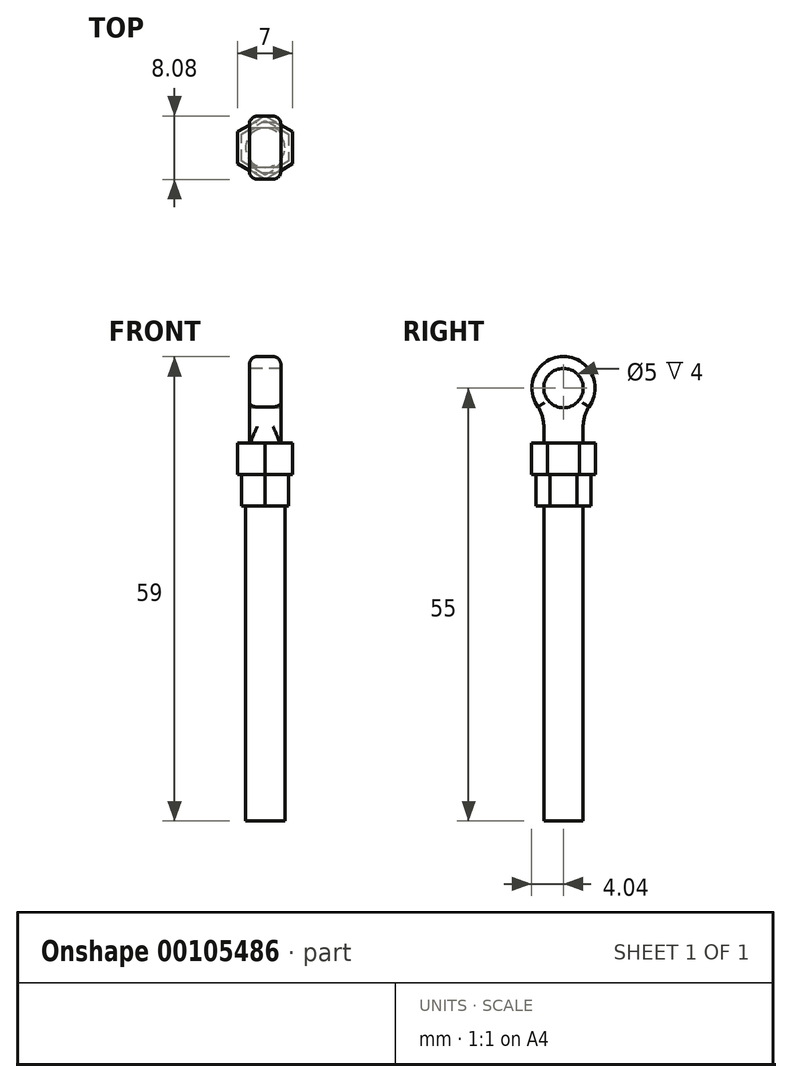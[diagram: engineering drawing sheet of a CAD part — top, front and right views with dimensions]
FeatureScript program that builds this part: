
annotation { "Feature Type Name" : "Feature", "Feature Type Description" : "" }
export const myFeature = defineFeature(function(context is Context, id is Id, definition is map)
    precondition{}
    {
        {
            var Q0;
            Q0=qCreatedBy(makeId("Top.planeOp"),FACE);
            var sketch = newSketch(context, id + "F0", { "sketchPlane" : qUnion([Q0])});
            skCircle(sketch, "E0", {"center": v(0, 0) * mm, "radius": 2.5 * mm});
            skSolve(sketch);
        }
        {
            var Q0;
            Q0=makeQuery(id+"F0.imprint","IMPRINT",FACE,{"disambiguationData":[TD([[makeQuery(id+"F0.imprint","IMPRINT",EDGE,{"derivedFrom":sQuery(id+"F0.wireOp",EDGE,"E0")}),1.0]])]});
            extrude(context, id + "F1", {"entities" : qUnion([Q0]), "depth" : 40 * mm});
        }
        {
            var Q0;
            Q0=makeQuery(id+"F1.opExtrude","CAP_FACE",FACE,{"disambiguationData":[OSD([sQuery(id+"F0.wireOp",EDGE,"E0")])],"isStart":false});
            var sketch = newSketch(context, id + "F2", { "sketchPlane" : qUnion([Q0])});
            skCircle(sketch, "E1.cCircle", {"center": v(0, 0) * mm, "radius": 3 * mm, "construction": true});
            skLineSegment(sketch, "E1.0", {"start": v(3, 1.73) * mm, "end": v(3, -1.73) * mm});
            skLineSegment(sketch, "E1.1", {"start": v(3, -1.73) * mm, "end": v(0, -3.46) * mm});
            skLineSegment(sketch, "E1.2", {"start": v(0, -3.46) * mm, "end": v(-3, -1.73) * mm});
            skLineSegment(sketch, "E1.3", {"start": v(-3, -1.73) * mm, "end": v(-3, 1.73) * mm});
            skLineSegment(sketch, "E1.4", {"start": v(-3, 1.73) * mm, "end": v(0, 3.46) * mm});
            skLineSegment(sketch, "E1.5", {"start": v(0, 3.46) * mm, "end": v(3, 1.73) * mm});
            skPoint(sketch, "E1.0.midPoint", {"position": v(3, 0) * mm});
            skSolve(sketch);
        }
        {
            var Q0;
            Q0=qSketchRegion(id+"F2",true);
            extrude(context, id + "F3", {"entities" : qUnion([Q0]), "operationType" : NewBodyOperationType.ADD, "depth" : 4 * mm});
        }
        {
            var Q0;
            Q0=makeQuery(id+"F3.opExtrude","CAP_FACE",FACE,{"disambiguationData":[OSD([sQuery(id+"F2.wireOp",EDGE,"E1.0"),sQuery(id+"F2.wireOp",EDGE,"E1.1"),sQuery(id+"F2.wireOp",EDGE,"E1.2"),sQuery(id+"F2.wireOp",EDGE,"E1.3"),sQuery(id+"F2.wireOp",EDGE,"E1.4"),sQuery(id+"F2.wireOp",EDGE,"E1.5")])],"isStart":false});
            var sketch = newSketch(context, id + "F4", { "sketchPlane" : qUnion([Q0])});
            skCircle(sketch, "E2.cCircle", {"center": v(0, 0) * mm, "radius": 3.5 * mm, "construction": true});
            skLineSegment(sketch, "E2.0", {"start": v(3.5, 2.02) * mm, "end": v(3.5, -2.02) * mm});
            skLineSegment(sketch, "E2.1", {"start": v(3.5, -2.02) * mm, "end": v(0, -4.04) * mm});
            skLineSegment(sketch, "E2.2", {"start": v(0, -4.04) * mm, "end": v(-3.5, -2.02) * mm});
            skLineSegment(sketch, "E2.3", {"start": v(-3.5, -2.02) * mm, "end": v(-3.5, 2.02) * mm});
            skLineSegment(sketch, "E2.4", {"start": v(-3.5, 2.02) * mm, "end": v(0, 4.04) * mm});
            skLineSegment(sketch, "E2.5", {"start": v(0, 4.04) * mm, "end": v(3.5, 2.02) * mm});
            skPoint(sketch, "E2.0.midPoint", {"position": v(3.5, 0) * mm});
            skSolve(sketch);
        }
        {
            var Q0;
            Q0=qSketchRegion(id+"F4",true);
            extrude(context, id + "F5", {"entities" : qUnion([Q0]), "operationType" : NewBodyOperationType.ADD, "depth" : 4 * mm});
        }
        {
            var Q0;
            Q0=qCreatedBy(makeId("Right.planeOp"),FACE);
            var sketch = newSketch(context, id + "F6", { "sketchPlane" : qUnion([Q0])});
            skCircle(sketch, "E3", {"center": v(0, 55) * mm, "radius": 2.5 * mm});
            skArc(sketch, "E4", {"start": v(3.2, 52.61) * mm, "mid": v(0, 59) * mm, "end": v(-3.2, 52.61) * mm});
            skLineSegment(sketch, "E5.top", {"start": v(-2.5, 46.12) * mm, "end": v(2.5, 46.12) * mm});
            skLineSegment(sketch, "E5.left", {"start": v(-2.5, 50.12) * mm, "end": v(-2.5, 46.12) * mm});
            skLineSegment(sketch, "E5.right", {"start": v(2.5, 50.12) * mm, "end": v(2.5, 46.12) * mm});
            skPoint(sketch, "E5.middle", {"position": v(0, 48.12) * mm});
            skArc(sketch, "E6", {"start": v(-2.5, 50.12) * mm, "mid": v(-2.68, 51.42) * mm, "end": v(-3.2, 52.61) * mm});
            skArc(sketch, "E7.MirrorCS", {"start": v(2.5, 50.12) * mm, "mid": v(2.68, 51.42) * mm, "end": v(3.2, 52.61) * mm});
            skSolve(sketch);
        }
        {
            var Q0;
            Q0=qSketchRegion(id+"F6",true);
            extrude(context, id + "F7", {"entities" : qUnion([Q0]), "operationType" : NewBodyOperationType.ADD, "endBound" : BoundingType.SYMMETRIC, "depth" : 4 * mm});
        }
        {
            var Q0;
            Q0=makeQuery(id+"F7.opExtrude","CAP_EDGE",EDGE,{"disambiguationData":[OSD([sQuery(id+"F6.wireOp",EDGE,"E4")])],"isStart":true});
            var Q1;
            Q1=makeQuery(id+"F7.opExtrude","CAP_EDGE",EDGE,{"disambiguationData":[OSD([sQuery(id+"F6.wireOp",EDGE,"E7.MirrorCS")])],"isStart":true});
            var Q2;
            Q2=makeQuery(id+"F7.opExtrude","CAP_EDGE",EDGE,{"disambiguationData":[OSD([sQuery(id+"F6.wireOp",EDGE,"E4")])],"isStart":false});
            var Q3;
            Q3=makeQuery(id+"F7.opExtrude","CAP_EDGE",EDGE,{"disambiguationData":[OSD([sQuery(id+"F6.wireOp",EDGE,"E7.MirrorCS")])],"isStart":false});
            fillet(context, id + "F8", {"entities" : qUnion([Q0, Q1, Q2, Q3]), "radius" : 1 * mm, "tangentPropagation" : true, "allowEdgeOverflow" : false});
        }
    });
